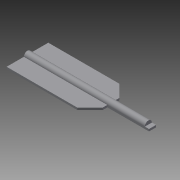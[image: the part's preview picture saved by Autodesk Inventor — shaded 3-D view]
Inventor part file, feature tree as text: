
AUTODESK INVENTOR PART (.ipt)
format: ipt  version: 2014 (Build 180170000, 170)  size: 96,256 bytes
history: native  units: mm
features: extrude x2, sketch x2, chamfer x1, plane x1, projected_geometry x1
ambient origin geometry x8: Origin, YZ Plane, XZ Plane, XY Plane, X Axis, Y Axis, Z Axis, Center Point
bodies: Body1 (feature_tree)
feature tree (7):
  extrude  "Extrusion3"  Depth=1.7mm
  chamfer  "Chamfer1"  Distance=10.0mm
  plane  "Work Plane1"
  extrude  "Extrusion4"  Depth=0.5mm TaperAngle=0.0deg
  sketch  "Sketch5"  dims[d11=10.0mm d12=1.7mm]
  sketch  "Sketch6"  dims[d13=20.0mm d14=10.0mm d15=0.5mm d16=0.0mm d17=3.0mm d18=2.0mm d19=45.0deg d20=-1.0mm d21=0.5mm d22=0.0mm]
  projected_geometry  "Project Cut Edges2"
